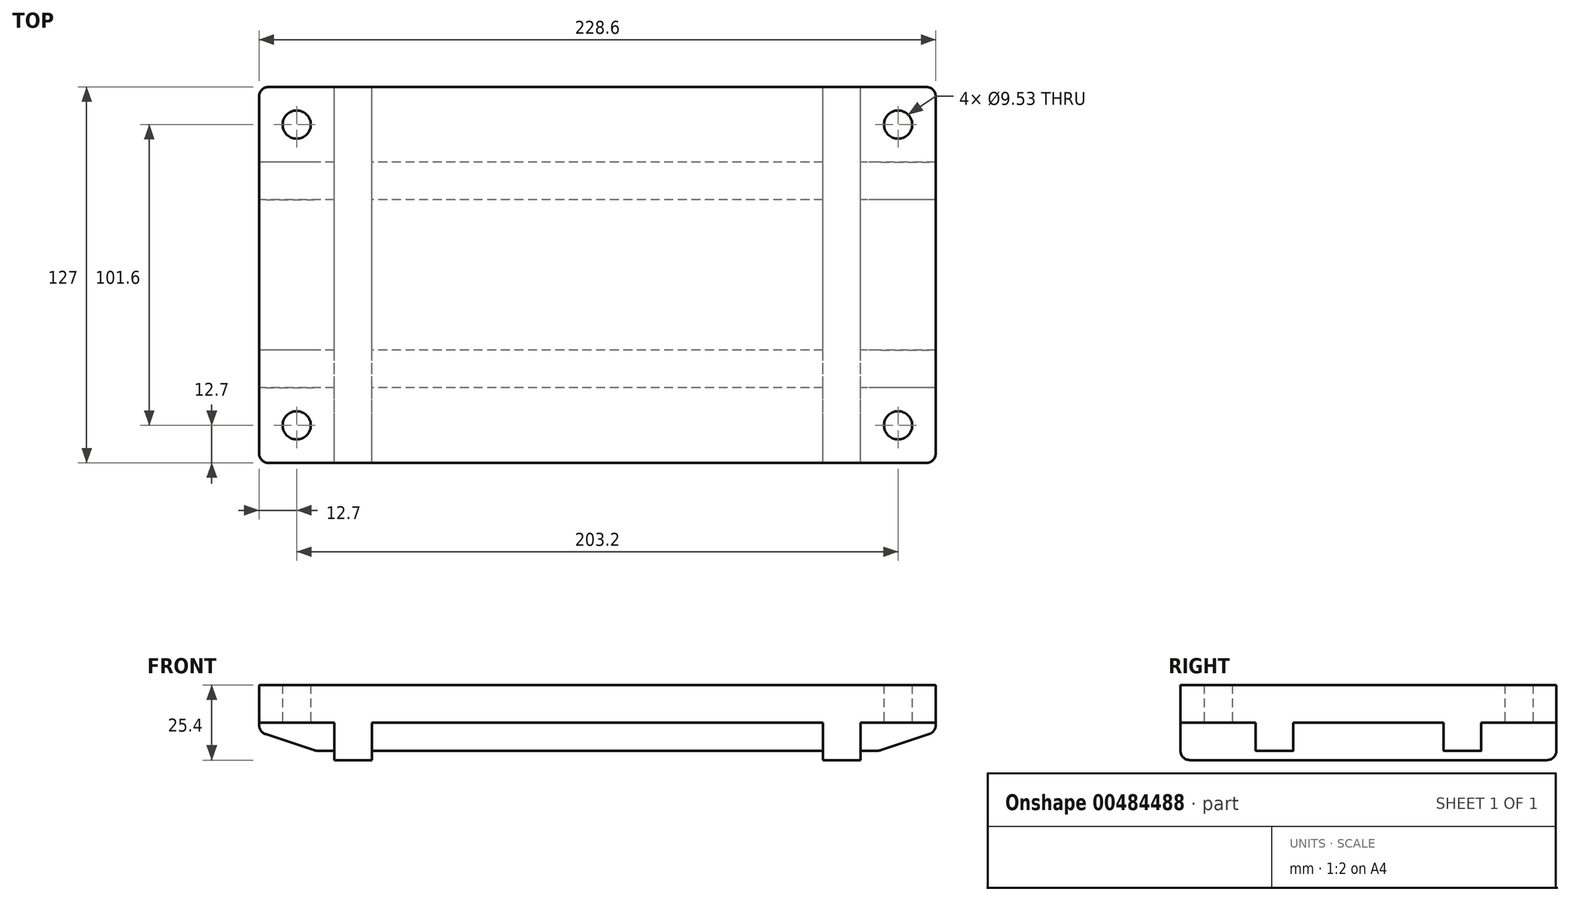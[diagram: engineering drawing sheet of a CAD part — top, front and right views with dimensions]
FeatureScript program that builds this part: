
annotation { "Feature Type Name" : "Feature", "Feature Type Description" : "" }
export const myFeature = defineFeature(function(context is Context, id is Id, definition is map)
    precondition{}
    {
        {
            var Q0;
            Q0=qCreatedBy(makeId("Top.planeOp"),FACE);
            var sketch = newSketch(context, id + "F0", { "sketchPlane" : qUnion([Q0])});
            skLineSegment(sketch, "E0.bottom", {"start": v(-114.3, 63.5) * mm, "end": v(114.3, 63.5) * mm});
            skLineSegment(sketch, "E0.top", {"start": v(-114.3, -63.5) * mm, "end": v(114.3, -63.5) * mm});
            skLineSegment(sketch, "E0.left", {"start": v(-114.3, 63.5) * mm, "end": v(-114.3, -63.5) * mm});
            skLineSegment(sketch, "E0.right", {"start": v(114.3, 63.5) * mm, "end": v(114.3, -63.5) * mm});
            skLineSegment(sketch, "E1.bottom", {"start": v(-101.6, 50.8) * mm, "end": v(101.6, 50.8) * mm, "construction": true});
            skLineSegment(sketch, "E1.top", {"start": v(-101.6, -50.8) * mm, "end": v(101.6, -50.8) * mm, "construction": true});
            skLineSegment(sketch, "E1.left", {"start": v(-101.6, 50.8) * mm, "end": v(-101.6, -50.8) * mm, "construction": true});
            skLineSegment(sketch, "E1.right", {"start": v(101.6, 50.8) * mm, "end": v(101.6, -50.8) * mm, "construction": true});
            skCircle(sketch, "E2", {"center": v(-101.6, 50.8) * mm, "radius": 4.76 * mm});
            skCircle(sketch, "E3", {"center": v(101.6, 50.8) * mm, "radius": 4.76 * mm});
            skCircle(sketch, "E4", {"center": v(101.6, -50.8) * mm, "radius": 4.76 * mm});
            skCircle(sketch, "E5", {"center": v(-101.6, -50.8) * mm, "radius": 4.76 * mm});
            skLineSegment(sketch, "E6", {"start": v(0, 50.8) * mm, "end": v(0, -50.8) * mm, "construction": true});
            skLineSegment(sketch, "E7", {"start": v(-114.3, 0) * mm, "end": v(114.3, 0) * mm, "construction": true});
            skSolve(sketch);
        }
        {
            var Q0;
            Q0=qSketchRegion(id+"F0",true);
            extrude(context, id + "F1", {"entities" : qUnion([Q0]), "depth" : 12.7 * mm});
        }
        {
            var Q0;
            Q0=makeQuery(id+"F1.opExtrude","CAP_FACE",FACE,{"disambiguationData":[OSD([sQuery(id+"F0.wireOp",EDGE,"E0.bottom"),sQuery(id+"F0.wireOp",EDGE,"E0.top"),sQuery(id+"F0.wireOp",EDGE,"E0.left"),sQuery(id+"F0.wireOp",EDGE,"E0.right"),sQuery(id+"F0.wireOp",EDGE,"E2"),sQuery(id+"F0.wireOp",EDGE,"E3"),sQuery(id+"F0.wireOp",EDGE,"E4"),sQuery(id+"F0.wireOp",EDGE,"E5")])],"isStart":true});
            var sketch = newSketch(context, id + "F2", { "sketchPlane" : qUnion([Q0])});
            skLineSegment(sketch, "E8.bottom", {"start": v(-88.9, 63.5) * mm, "end": v(-76.2, 63.5) * mm});
            skLineSegment(sketch, "E8.top", {"start": v(-88.9, -63.5) * mm, "end": v(-76.2, -63.5) * mm});
            skLineSegment(sketch, "E8.left", {"start": v(-88.9, 63.5) * mm, "end": v(-88.9, -63.5) * mm});
            skLineSegment(sketch, "E8.right", {"start": v(-76.2, 63.5) * mm, "end": v(-76.2, -63.5) * mm});
            skLineSegment(sketch, "E9.bottom", {"start": v(76.2, 63.5) * mm, "end": v(88.9, 63.5) * mm});
            skLineSegment(sketch, "E9.top", {"start": v(76.2, -63.5) * mm, "end": v(88.9, -63.5) * mm});
            skLineSegment(sketch, "E9.left", {"start": v(76.2, 63.5) * mm, "end": v(76.2, -63.5) * mm});
            skLineSegment(sketch, "E9.right", {"start": v(88.9, 63.5) * mm, "end": v(88.9, -63.5) * mm});
            skLineSegment(sketch, "E10", {"start": v(-76.2, 0) * mm, "end": v(76.2, 0) * mm, "construction": true});
            skSolve(sketch);
        }
        {
            var Q0;
            Q0 = qSketchRegion(id + "F2", true);
            extrude(context, id + "F3", {"entities" : qUnion([Q0]), "operationType" : NewBodyOperationType.ADD, "depth" : 12.7 * mm});
        }
        {
            var Q0;
            {var subQ0=sQuery(id+"F0.wireOp",EDGE,"E0.top");var subQ1=sQuery(id+"F0.wireOp",EDGE,"E0.bottom");Q0=makeQuery(id+"F3.boolean.opBoolean","SPLIT",FACE,{"disambiguationData":[TD([makeQuery(id+"F3.opExtrude","SWEPT_FACE",FACE,{"disambiguationData":[OSD([sQuery(id+"F2.wireOp",EDGE,"E8.right")])]})])],"derivedFrom":makeQuery(id+"F1.opExtrude","CAP_FACE",FACE,{"disambiguationData":[OSD([subQ1,subQ0,sQuery(id+"F0.wireOp",EDGE,"E0.left"),sQuery(id+"F0.wireOp",EDGE,"E0.right"),sQuery(id+"F0.wireOp",EDGE,"E2"),sQuery(id+"F0.wireOp",EDGE,"E3"),sQuery(id+"F0.wireOp",EDGE,"E4"),sQuery(id+"F0.wireOp",EDGE,"E5")])],"isStart":true})});}
            var sketch = newSketch(context, id + "F4", { "sketchPlane" : qUnion([Q0])});
            skLineSegment(sketch, "E11.bottom", {"start": v(114.3, -38.1) * mm, "end": v(-114.3, -38.1) * mm});
            skLineSegment(sketch, "E11.top", {"start": v(114.3, -25.4) * mm, "end": v(-114.3, -25.4) * mm});
            skLineSegment(sketch, "E11.left", {"start": v(114.3, -38.1) * mm, "end": v(114.3, -25.4) * mm});
            skLineSegment(sketch, "E11.right", {"start": v(-114.3, -38.1) * mm, "end": v(-114.3, -25.4) * mm});
            skLineSegment(sketch, "E12.bottom", {"start": v(114.3, 25.4) * mm, "end": v(-114.3, 25.4) * mm});
            skLineSegment(sketch, "E12.top", {"start": v(114.3, 38.1) * mm, "end": v(-114.3, 38.1) * mm});
            skLineSegment(sketch, "E12.left", {"start": v(114.3, 25.4) * mm, "end": v(114.3, 38.1) * mm});
            skLineSegment(sketch, "E12.right", {"start": v(-114.3, 25.4) * mm, "end": v(-114.3, 38.1) * mm});
            skLineSegment(sketch, "E13", {"start": v(0, 25.4) * mm, "end": v(0, -25.4) * mm, "construction": true});
            skSolve(sketch);
        }
        {
            var Q0;
            Q0 = qSketchRegion(id + "F4", true);
            extrude(context, id + "F5", {"entities" : qUnion([Q0]), "operationType" : NewBodyOperationType.ADD, "depth" : 9.52 * mm});
        }
        {
            var Q0;
            Q0=makeQuery(id+"F5.opExtrude","CAP_EDGE",EDGE,{"disambiguationData":[OSD([sQuery(id+"F4.wireOp",EDGE,"E12.right")])],"isStart":false});
            var Q1;
            Q1=makeQuery(id+"F5.opExtrude","CAP_EDGE",EDGE,{"disambiguationData":[OSD([sQuery(id+"F4.wireOp",EDGE,"E11.right")])],"isStart":false});
            chamfer(context, id + "F6", {"entities" : qUnion([Q0, Q1]), "chamferType" : ChamferType.TWO_OFFSETS, "width1" : 6.35 * mm, "oppositeDirection" : false, "width2" : 19.05 * mm, "tangentPropagation" : true});
        }
        {
            var Q0;
            {var subQ0=sQuery(id+"F4.wireOp",EDGE,"E12.right");Q0=makeQuery(id+"F6.opChamfer","BLEND_EDGE",EDGE,{"blendedFrom":[makeQuery(id+"F5.opExtrude","CAP_EDGE",EDGE,{"disambiguationData":[OSD([subQ0])],"isStart":false}),makeQuery(id+"F5.boolean.opBoolean","MERGE",FACE,{"derivedFrom":[makeQuery(id+"F1.opExtrude","SWEPT_FACE",FACE,{"disambiguationData":[OSD([sQuery(id+"F0.wireOp",EDGE,"E0.left")])]}),makeQuery(id+"F5.opExtrude","SWEPT_FACE",FACE,{"disambiguationData":[OSD([sQuery(id+"F4.wireOp",EDGE,"E11.right")])]}),makeQuery(id+"F5.opExtrude","SWEPT_FACE",FACE,{"disambiguationData":[OSD([subQ0])]})]})],"blendedInto":[makeQuery(id+"F5.boolean.opBoolean","MERGE",FACE,{"derivedFrom":[makeQuery(id+"F1.opExtrude","SWEPT_FACE",FACE,{"disambiguationData":[OSD([sQuery(id+"F0.wireOp",EDGE,"E0.left")])]}),makeQuery(id+"F5.opExtrude","SWEPT_FACE",FACE,{"disambiguationData":[OSD([sQuery(id+"F4.wireOp",EDGE,"E11.right")])]}),makeQuery(id+"F5.opExtrude","SWEPT_FACE",FACE,{"disambiguationData":[OSD([subQ0])]})]})]});}
            var Q1;
            {var subQ0=sQuery(id+"F4.wireOp",EDGE,"E11.right");Q1=makeQuery(id+"F6.opChamfer","BLEND_EDGE",EDGE,{"blendedFrom":[makeQuery(id+"F5.opExtrude","CAP_EDGE",EDGE,{"disambiguationData":[OSD([subQ0])],"isStart":false}),makeQuery(id+"F5.boolean.opBoolean","MERGE",FACE,{"derivedFrom":[makeQuery(id+"F1.opExtrude","SWEPT_FACE",FACE,{"disambiguationData":[OSD([sQuery(id+"F0.wireOp",EDGE,"E0.left")])]}),makeQuery(id+"F5.opExtrude","SWEPT_FACE",FACE,{"disambiguationData":[OSD([subQ0])]}),makeQuery(id+"F5.opExtrude","SWEPT_FACE",FACE,{"disambiguationData":[OSD([sQuery(id+"F4.wireOp",EDGE,"E12.right")])]})]})],"blendedInto":[makeQuery(id+"F5.boolean.opBoolean","MERGE",FACE,{"derivedFrom":[makeQuery(id+"F1.opExtrude","SWEPT_FACE",FACE,{"disambiguationData":[OSD([sQuery(id+"F0.wireOp",EDGE,"E0.left")])]}),makeQuery(id+"F5.opExtrude","SWEPT_FACE",FACE,{"disambiguationData":[OSD([subQ0])]}),makeQuery(id+"F5.opExtrude","SWEPT_FACE",FACE,{"disambiguationData":[OSD([sQuery(id+"F4.wireOp",EDGE,"E12.right")])]})]})]});}
            var Q2;
            {var subQ0=sQuery(id+"F4.wireOp",EDGE,"E12.bottom");var subQ1=sQuery(id+"F4.wireOp",EDGE,"E12.top");var subQ2=sQuery(id+"F4.wireOp",EDGE,"E12.right");Q2=makeQuery(id+"F6.opChamfer","BLEND_EDGE",EDGE,{"blendedFrom":[makeQuery(id+"F5.opExtrude","CAP_EDGE",EDGE,{"disambiguationData":[OSD([subQ2])],"isStart":false}),makeQuery(id+"F5.boolean.opBoolean","SPLIT",FACE,{"disambiguationData":[TD([makeQuery(id+"F1.opExtrude","SWEPT_FACE",FACE,{"disambiguationData":[OSD([sQuery(id+"F0.wireOp",EDGE,"E0.left")])]})])],"derivedFrom":makeQuery(id+"F5.opExtrude","CAP_FACE",FACE,{"disambiguationData":[OSD([subQ0,subQ1,sQuery(id+"F4.wireOp",EDGE,"E12.left"),subQ2])],"isStart":false})})],"blendedInto":[makeQuery(id+"F5.boolean.opBoolean","SPLIT",FACE,{"disambiguationData":[TD([makeQuery(id+"F1.opExtrude","SWEPT_FACE",FACE,{"disambiguationData":[OSD([sQuery(id+"F0.wireOp",EDGE,"E0.left")])]})])],"derivedFrom":makeQuery(id+"F5.opExtrude","CAP_FACE",FACE,{"disambiguationData":[OSD([subQ0,subQ1,sQuery(id+"F4.wireOp",EDGE,"E12.left"),subQ2])],"isStart":false})})]});}
            var Q3;
            {var subQ0=sQuery(id+"F4.wireOp",EDGE,"E11.top");var subQ1=sQuery(id+"F4.wireOp",EDGE,"E11.bottom");var subQ2=sQuery(id+"F4.wireOp",EDGE,"E11.right");Q3=makeQuery(id+"F6.opChamfer","BLEND_EDGE",EDGE,{"blendedFrom":[makeQuery(id+"F5.opExtrude","CAP_EDGE",EDGE,{"disambiguationData":[OSD([subQ2])],"isStart":false}),makeQuery(id+"F5.boolean.opBoolean","SPLIT",FACE,{"disambiguationData":[TD([makeQuery(id+"F1.opExtrude","SWEPT_FACE",FACE,{"disambiguationData":[OSD([sQuery(id+"F0.wireOp",EDGE,"E0.left")])]})])],"derivedFrom":makeQuery(id+"F5.opExtrude","CAP_FACE",FACE,{"disambiguationData":[OSD([subQ1,subQ0,sQuery(id+"F4.wireOp",EDGE,"E11.left"),subQ2])],"isStart":false})})],"blendedInto":[makeQuery(id+"F5.boolean.opBoolean","SPLIT",FACE,{"disambiguationData":[TD([makeQuery(id+"F1.opExtrude","SWEPT_FACE",FACE,{"disambiguationData":[OSD([sQuery(id+"F0.wireOp",EDGE,"E0.left")])]})])],"derivedFrom":makeQuery(id+"F5.opExtrude","CAP_FACE",FACE,{"disambiguationData":[OSD([subQ1,subQ0,sQuery(id+"F4.wireOp",EDGE,"E11.left"),subQ2])],"isStart":false})})]});}
            fillet(context, id + "F7", {"entities" : qUnion([Q0, Q1, Q2, Q3]), "radius" : 3.17 * mm, "tangentPropagation" : true, "allowEdgeOverflow" : false});
        }
        {
            var Q0;
            Q0=makeQuery(id+"F3.opExtrude","CAP_EDGE",EDGE,{"disambiguationData":[OSD([sQuery(id+"F2.wireOp",EDGE,"E8.bottom")])],"isStart":false});
            var Q1;
            Q1=makeQuery(id+"F3.opExtrude","CAP_EDGE",EDGE,{"disambiguationData":[OSD([sQuery(id+"F2.wireOp",EDGE,"E8.top")])],"isStart":false});
            var Q2;
            Q2=makeQuery(id+"F3.opExtrude","CAP_EDGE",EDGE,{"disambiguationData":[OSD([sQuery(id+"F2.wireOp",EDGE,"E9.top")])],"isStart":false});
            var Q3;
            Q3=makeQuery(id+"F3.opExtrude","CAP_EDGE",EDGE,{"disambiguationData":[OSD([sQuery(id+"F2.wireOp",EDGE,"E9.bottom")])],"isStart":false});
            fillet(context, id + "F8", {"entities" : qUnion([Q0, Q1, Q2, Q3]), "radius" : 3.17 * mm, "tangentPropagation" : true, "allowEdgeOverflow" : false});
        }
        {
            var Q0;
            Q0=makeQuery(id+"F5.opExtrude","CAP_EDGE",EDGE,{"disambiguationData":[OSD([sQuery(id+"F4.wireOp",EDGE,"E12.left")])],"isStart":false});
            var Q1;
            Q1=makeQuery(id+"F5.opExtrude","CAP_EDGE",EDGE,{"disambiguationData":[OSD([sQuery(id+"F4.wireOp",EDGE,"E11.left")])],"isStart":false});
            chamfer(context, id + "F9", {"entities" : qUnion([Q0, Q1]), "chamferType" : ChamferType.TWO_OFFSETS, "width1" : 19.05 * mm, "oppositeDirection" : false, "width2" : 6.35 * mm, "tangentPropagation" : true});
        }
        {
            var Q0;
            {var subQ0=sQuery(id+"F4.wireOp",EDGE,"E12.left");Q0=makeQuery(id+"F9.opChamfer","BLEND_EDGE",EDGE,{"blendedFrom":[makeQuery(id+"F5.opExtrude","CAP_EDGE",EDGE,{"disambiguationData":[OSD([subQ0])],"isStart":false}),makeQuery(id+"F5.boolean.opBoolean","MERGE",FACE,{"derivedFrom":[makeQuery(id+"F1.opExtrude","SWEPT_FACE",FACE,{"disambiguationData":[OSD([sQuery(id+"F0.wireOp",EDGE,"E0.right")])]}),makeQuery(id+"F5.opExtrude","SWEPT_FACE",FACE,{"disambiguationData":[OSD([sQuery(id+"F4.wireOp",EDGE,"E11.left")])]}),makeQuery(id+"F5.opExtrude","SWEPT_FACE",FACE,{"disambiguationData":[OSD([subQ0])]})]})],"blendedInto":[makeQuery(id+"F5.boolean.opBoolean","MERGE",FACE,{"derivedFrom":[makeQuery(id+"F1.opExtrude","SWEPT_FACE",FACE,{"disambiguationData":[OSD([sQuery(id+"F0.wireOp",EDGE,"E0.right")])]}),makeQuery(id+"F5.opExtrude","SWEPT_FACE",FACE,{"disambiguationData":[OSD([sQuery(id+"F4.wireOp",EDGE,"E11.left")])]}),makeQuery(id+"F5.opExtrude","SWEPT_FACE",FACE,{"disambiguationData":[OSD([subQ0])]})]})]});}
            var Q1;
            {var subQ0=sQuery(id+"F4.wireOp",EDGE,"E11.left");Q1=makeQuery(id+"F9.opChamfer","BLEND_EDGE",EDGE,{"blendedFrom":[makeQuery(id+"F5.opExtrude","CAP_EDGE",EDGE,{"disambiguationData":[OSD([subQ0])],"isStart":false}),makeQuery(id+"F5.boolean.opBoolean","MERGE",FACE,{"derivedFrom":[makeQuery(id+"F1.opExtrude","SWEPT_FACE",FACE,{"disambiguationData":[OSD([sQuery(id+"F0.wireOp",EDGE,"E0.right")])]}),makeQuery(id+"F5.opExtrude","SWEPT_FACE",FACE,{"disambiguationData":[OSD([subQ0])]}),makeQuery(id+"F5.opExtrude","SWEPT_FACE",FACE,{"disambiguationData":[OSD([sQuery(id+"F4.wireOp",EDGE,"E12.left")])]})]})],"blendedInto":[makeQuery(id+"F5.boolean.opBoolean","MERGE",FACE,{"derivedFrom":[makeQuery(id+"F1.opExtrude","SWEPT_FACE",FACE,{"disambiguationData":[OSD([sQuery(id+"F0.wireOp",EDGE,"E0.right")])]}),makeQuery(id+"F5.opExtrude","SWEPT_FACE",FACE,{"disambiguationData":[OSD([subQ0])]}),makeQuery(id+"F5.opExtrude","SWEPT_FACE",FACE,{"disambiguationData":[OSD([sQuery(id+"F4.wireOp",EDGE,"E12.left")])]})]})]});}
            var Q2;
            {var subQ0=sQuery(id+"F4.wireOp",EDGE,"E11.bottom");var subQ1=sQuery(id+"F4.wireOp",EDGE,"E11.top");var subQ2=sQuery(id+"F4.wireOp",EDGE,"E11.left");Q2=makeQuery(id+"F9.opChamfer","BLEND_EDGE",EDGE,{"blendedFrom":[makeQuery(id+"F5.opExtrude","CAP_EDGE",EDGE,{"disambiguationData":[OSD([subQ2])],"isStart":false}),makeQuery(id+"F5.boolean.opBoolean","SPLIT",FACE,{"disambiguationData":[TD([makeQuery(id+"F1.opExtrude","SWEPT_FACE",FACE,{"disambiguationData":[OSD([sQuery(id+"F0.wireOp",EDGE,"E0.right")])]})])],"derivedFrom":makeQuery(id+"F5.opExtrude","CAP_FACE",FACE,{"disambiguationData":[OSD([subQ0,subQ1,subQ2,sQuery(id+"F4.wireOp",EDGE,"E11.right")])],"isStart":false})})],"blendedInto":[makeQuery(id+"F5.boolean.opBoolean","SPLIT",FACE,{"disambiguationData":[TD([makeQuery(id+"F1.opExtrude","SWEPT_FACE",FACE,{"disambiguationData":[OSD([sQuery(id+"F0.wireOp",EDGE,"E0.right")])]})])],"derivedFrom":makeQuery(id+"F5.opExtrude","CAP_FACE",FACE,{"disambiguationData":[OSD([subQ0,subQ1,subQ2,sQuery(id+"F4.wireOp",EDGE,"E11.right")])],"isStart":false})})]});}
            var Q3;
            {var subQ0=sQuery(id+"F4.wireOp",EDGE,"E12.bottom");var subQ1=sQuery(id+"F4.wireOp",EDGE,"E12.left");var subQ2=sQuery(id+"F4.wireOp",EDGE,"E12.top");Q3=makeQuery(id+"F9.opChamfer","BLEND_EDGE",EDGE,{"blendedFrom":[makeQuery(id+"F5.opExtrude","CAP_EDGE",EDGE,{"disambiguationData":[OSD([subQ1])],"isStart":false}),makeQuery(id+"F5.boolean.opBoolean","SPLIT",FACE,{"disambiguationData":[TD([makeQuery(id+"F1.opExtrude","SWEPT_FACE",FACE,{"disambiguationData":[OSD([sQuery(id+"F0.wireOp",EDGE,"E0.right")])]})])],"derivedFrom":makeQuery(id+"F5.opExtrude","CAP_FACE",FACE,{"disambiguationData":[OSD([subQ0,subQ2,subQ1,sQuery(id+"F4.wireOp",EDGE,"E12.right")])],"isStart":false})})],"blendedInto":[makeQuery(id+"F5.boolean.opBoolean","SPLIT",FACE,{"disambiguationData":[TD([makeQuery(id+"F1.opExtrude","SWEPT_FACE",FACE,{"disambiguationData":[OSD([sQuery(id+"F0.wireOp",EDGE,"E0.right")])]})])],"derivedFrom":makeQuery(id+"F5.opExtrude","CAP_FACE",FACE,{"disambiguationData":[OSD([subQ0,subQ2,subQ1,sQuery(id+"F4.wireOp",EDGE,"E12.right")])],"isStart":false})})]});}
            fillet(context, id + "F10", {"entities" : qUnion([Q0, Q1, Q2, Q3]), "radius" : 3.17 * mm, "tangentPropagation" : true, "allowEdgeOverflow" : false});
        }
        {
            var Q0;
            Q0=makeQuery(id+"F1.opExtrude","SWEPT_EDGE",EDGE,{"disambiguationData":[OSD([sQuery(id+"F0.wireOp",EDGE,"E0.top"),sQuery(id+"F0.wireOp",EDGE,"E0.left")])]});
            var Q1;
            Q1=makeQuery(id+"F1.opExtrude","SWEPT_EDGE",EDGE,{"disambiguationData":[OSD([sQuery(id+"F0.wireOp",EDGE,"E0.bottom"),sQuery(id+"F0.wireOp",EDGE,"E0.left")])]});
            var Q2;
            Q2=makeQuery(id+"F1.opExtrude","SWEPT_EDGE",EDGE,{"disambiguationData":[OSD([sQuery(id+"F0.wireOp",EDGE,"E0.top"),sQuery(id+"F0.wireOp",EDGE,"E0.right")])]});
            var Q3;
            Q3=makeQuery(id+"F1.opExtrude","SWEPT_EDGE",EDGE,{"disambiguationData":[OSD([sQuery(id+"F0.wireOp",EDGE,"E0.bottom"),sQuery(id+"F0.wireOp",EDGE,"E0.right")])]});
            fillet(context, id + "F11", {"entities" : qUnion([Q0, Q1, Q2, Q3]), "radius" : 3.17 * mm, "tangentPropagation" : true, "allowEdgeOverflow" : false});
        }
    });
